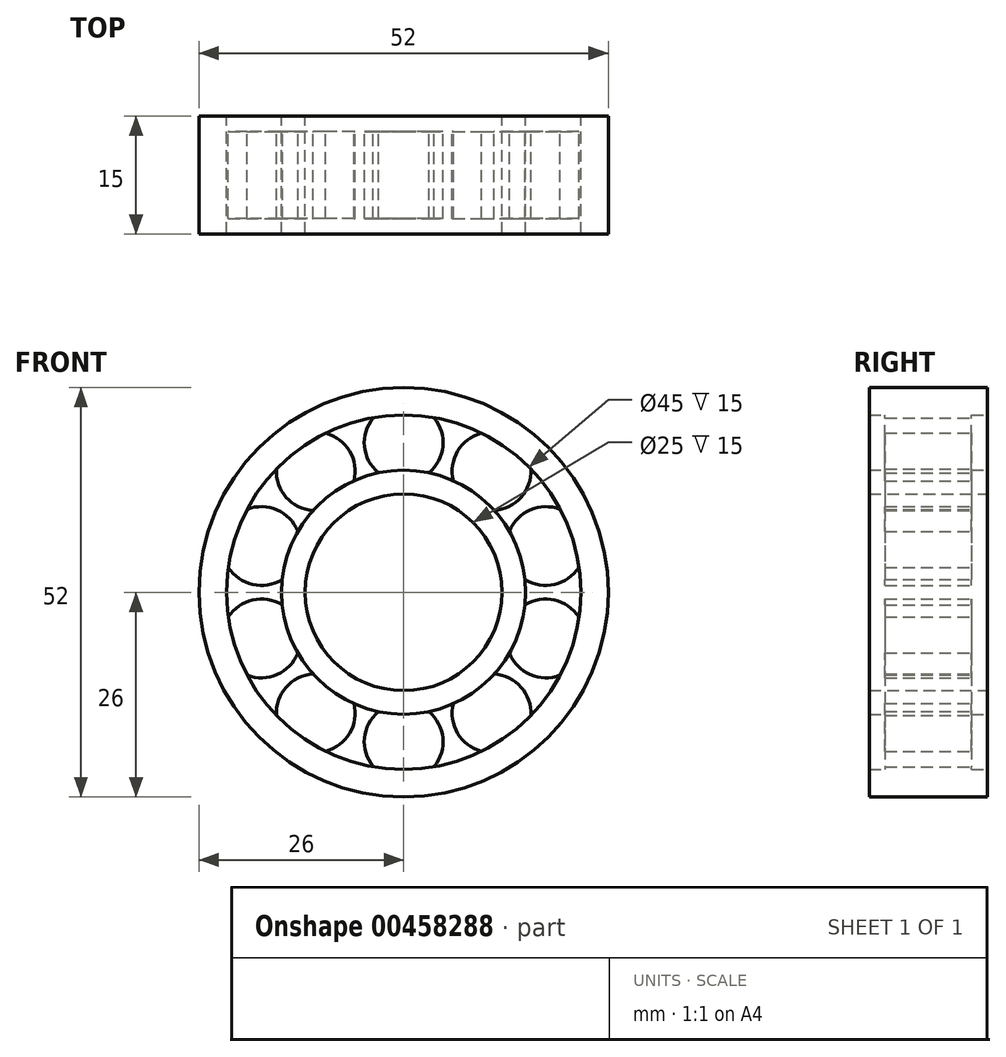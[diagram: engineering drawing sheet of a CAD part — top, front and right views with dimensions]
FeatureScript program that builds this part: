
annotation { "Feature Type Name" : "Feature", "Feature Type Description" : "" }
export const myFeature = defineFeature(function(context is Context, id is Id, definition is map)
    precondition{}
    {
        {
            var Q0;
            Q0=qCreatedBy(makeId("Front.planeOp"),FACE);
            var sketch = newSketch(context, id + "F0", { "sketchPlane" : qUnion([Q0])});
            skCircle(sketch, "E0", {"center": v(0, 0) * mm, "radius": 26 * mm});
            skCircle(sketch, "E1", {"center": v(0, 0) * mm, "radius": 22.5 * mm});
            skCircle(sketch, "E2", {"center": v(0, 0) * mm, "radius": 12.5 * mm});
            skCircle(sketch, "E3", {"center": v(0, 0) * mm, "radius": 15.5 * mm});
            skSolve(sketch);
        }
        {
            var Q0;
            Q0=makeQuery(id+"F0.imprint","IMPRINT",FACE,{"disambiguationData":[TD([[makeQuery(id+"F0.imprint","IMPRINT",EDGE,{"derivedFrom":sQuery(id+"F0.wireOp",EDGE,"E0")}),1.0]])]});
            var Q1;
            Q1=makeQuery(id+"F0.imprint","IMPRINT",FACE,{"disambiguationData":[TD([[makeQuery(id+"F0.imprint","IMPRINT",EDGE,{"derivedFrom":sQuery(id+"F0.wireOp",EDGE,"E2")}),-1.0]])]});
            extrude(context, id + "F1", {"entities" : qUnion([Q0, Q1]), "depth" : 15 * mm});
        }
        {
            var Q0;
            Q0=qCreatedBy(makeId("Front.planeOp"),FACE);
            cPlane(context, id + "F2", {"entities" : qUnion([Q0]), "cplaneType" : CPlaneType.OFFSET, "offset" : 2 * mm, "width" : 150 * mm, "height" : 150 * mm});
        }
        {
            var Q0;
            Q0=qCreatedBy(id+"F2.planeOp",FACE);
            var sketch = newSketch(context, id + "F3", { "sketchPlane" : qUnion([Q0])});
            skCircle(sketch, "E4", {"center": v(0, 19) * mm, "radius": 5 * mm});
            skCircle(sketch, "E5.1.0", {"center": v(-11.17, 15.37) * mm, "radius": 5 * mm});
            skCircle(sketch, "E5.2.0", {"center": v(-18.07, 5.87) * mm, "radius": 5 * mm});
            skCircle(sketch, "E5.3.0", {"center": v(-18.07, -5.87) * mm, "radius": 5 * mm});
            skCircle(sketch, "E5.4.0", {"center": v(-11.17, -15.37) * mm, "radius": 5 * mm});
            skCircle(sketch, "E5.5.0", {"center": v(0, -19) * mm, "radius": 5 * mm});
            skCircle(sketch, "E5.6.0", {"center": v(11.17, -15.37) * mm, "radius": 5 * mm});
            skCircle(sketch, "E5.7.0", {"center": v(18.07, -5.87) * mm, "radius": 5 * mm});
            skCircle(sketch, "E5.8.0", {"center": v(18.07, 5.87) * mm, "radius": 5 * mm});
            skCircle(sketch, "E5.9.0", {"center": v(11.17, 15.37) * mm, "radius": 5 * mm});
            skPoint(sketch, "E5.center", {"position": v(0, 0) * mm});
            skSolve(sketch);
        }
        {
            var Q0;
            Q0=makeQuery(id+"F3.imprint","IMPRINT",FACE,{"disambiguationData":[TD([[makeQuery(id+"F3.imprint","IMPRINT",EDGE,{"derivedFrom":sQuery(id+"F3.wireOp",EDGE,"E4")}),1.0]])]});
            var Q1;
            Q1=makeQuery(id+"F3.imprint","IMPRINT",FACE,{"disambiguationData":[TD([[makeQuery(id+"F3.imprint","IMPRINT",EDGE,{"derivedFrom":sQuery(id+"F3.wireOp",EDGE,"E5.9.0")}),1.0]])]});
            var Q2;
            Q2=makeQuery(id+"F3.imprint","IMPRINT",FACE,{"disambiguationData":[TD([[makeQuery(id+"F3.imprint","IMPRINT",EDGE,{"derivedFrom":sQuery(id+"F3.wireOp",EDGE,"E5.8.0")}),1.0]])]});
            var Q3;
            Q3=makeQuery(id+"F3.imprint","IMPRINT",FACE,{"disambiguationData":[TD([[makeQuery(id+"F3.imprint","IMPRINT",EDGE,{"derivedFrom":sQuery(id+"F3.wireOp",EDGE,"E5.7.0")}),1.0]])]});
            var Q4;
            Q4=makeQuery(id+"F3.imprint","IMPRINT",FACE,{"disambiguationData":[TD([[makeQuery(id+"F3.imprint","IMPRINT",EDGE,{"derivedFrom":sQuery(id+"F3.wireOp",EDGE,"E5.6.0")}),1.0]])]});
            var Q5;
            Q5=makeQuery(id+"F3.imprint","IMPRINT",FACE,{"disambiguationData":[TD([[makeQuery(id+"F3.imprint","IMPRINT",EDGE,{"derivedFrom":sQuery(id+"F3.wireOp",EDGE,"E5.5.0")}),1.0]])]});
            var Q6;
            Q6=makeQuery(id+"F3.imprint","IMPRINT",FACE,{"disambiguationData":[TD([[makeQuery(id+"F3.imprint","IMPRINT",EDGE,{"derivedFrom":sQuery(id+"F3.wireOp",EDGE,"E5.4.0")}),1.0]])]});
            var Q7;
            Q7=makeQuery(id+"F3.imprint","IMPRINT",FACE,{"disambiguationData":[TD([[makeQuery(id+"F3.imprint","IMPRINT",EDGE,{"derivedFrom":sQuery(id+"F3.wireOp",EDGE,"E5.3.0")}),1.0]])]});
            var Q8;
            Q8=makeQuery(id+"F3.imprint","IMPRINT",FACE,{"disambiguationData":[TD([[makeQuery(id+"F3.imprint","IMPRINT",EDGE,{"derivedFrom":sQuery(id+"F3.wireOp",EDGE,"E5.2.0")}),1.0]])]});
            var Q9;
            Q9=makeQuery(id+"F3.imprint","IMPRINT",FACE,{"disambiguationData":[TD([[makeQuery(id+"F3.imprint","IMPRINT",EDGE,{"derivedFrom":sQuery(id+"F3.wireOp",EDGE,"E5.1.0")}),1.0]])]});
            extrude(context, id + "F4", {"entities" : qUnion([Q0, Q1, Q2, Q3, Q4, Q5, Q6, Q7, Q8, Q9]), "operationType" : NewBodyOperationType.ADD, "depth" : 11 * mm});
        }
    });
